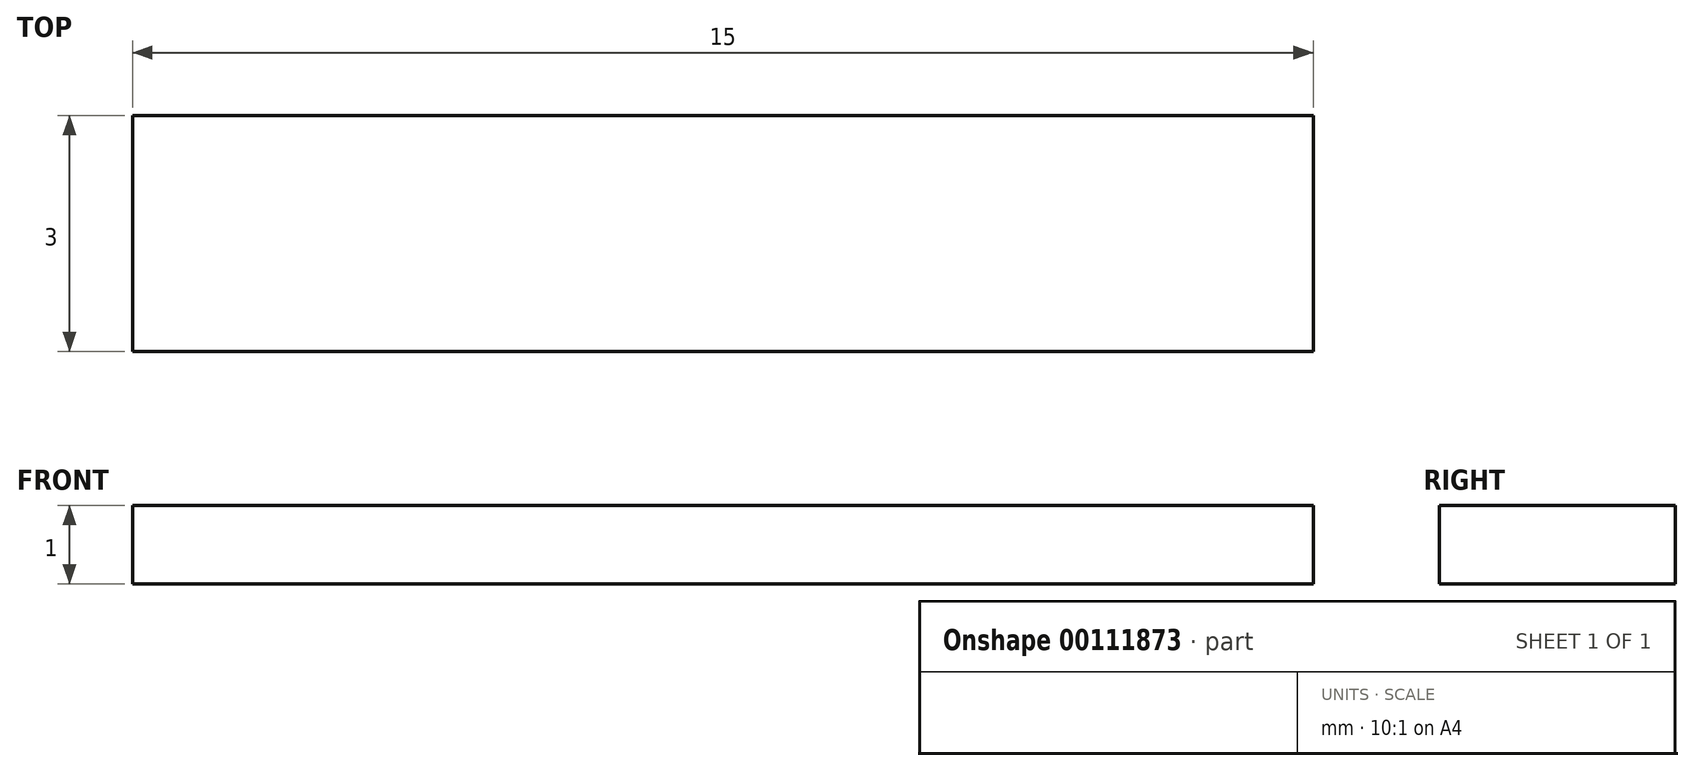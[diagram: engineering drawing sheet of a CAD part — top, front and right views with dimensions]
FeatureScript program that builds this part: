
annotation { "Feature Type Name" : "Feature", "Feature Type Description" : "" }
export const myFeature = defineFeature(function(context is Context, id is Id, definition is map)
    precondition{}
    {
        {
            var Q0;
            Q0=qCreatedBy(makeId("Top.planeOp"),FACE);
            var sketch = newSketch(context, id + "F0", { "sketchPlane" : qUnion([Q0])});
            skLineSegment(sketch, "E0.bottom", {"start": v(-7.5, 1.5) * mm, "end": v(7.5, 1.5) * mm});
            skLineSegment(sketch, "E0.top", {"start": v(-7.5, -1.5) * mm, "end": v(7.5, -1.5) * mm});
            skLineSegment(sketch, "E0.left", {"start": v(-7.5, 1.5) * mm, "end": v(-7.5, -1.5) * mm});
            skLineSegment(sketch, "E0.right", {"start": v(7.5, 1.5) * mm, "end": v(7.5, -1.5) * mm});
            skSolve(sketch);
        }
        {
            var Q0;
            Q0=makeQuery(id+"F0.imprint","IMPRINT",FACE,{"disambiguationData":[TD([[makeQuery(id+"F0.imprint","IMPRINT",EDGE,{"derivedFrom":sQuery(id+"F0.wireOp",EDGE,"E0.bottom")}),-1.0]])]});
            extrude(context, id + "F1", {"entities" : qUnion([Q0]), "depth" : 1 * mm});
        }
    });
